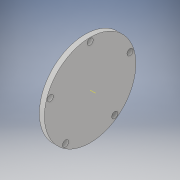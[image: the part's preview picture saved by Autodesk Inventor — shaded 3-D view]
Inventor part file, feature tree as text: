
AUTODESK INVENTOR PART (.ipt)
format: ipt  version: 2018 (Build 220112000, 112)  size: 112,128 bytes
history: native  units: in
note: dims shown in document units (in); Inventor stores cm internally (conversion verified against a paired STEP export)
features: extrude x2, sketch x2, other x1, pattern_circular x1
ambient origin geometry x8: Origin, YZ Plane, XZ Plane, XY Plane, X Axis, Y Axis, Z Axis, Center Point
bodies: Solid1 (feature_tree)
feature tree (6):
  extrude  "Extrusion1"  Depth=0.3937in TaperAngle=0.0deg
  extrude  "Extrusion2"  Depth=0.3937in
  other  "Work Axis1"
  pattern_circular  "Circular Pattern1"  [2 undecoded]
  sketch  "Sketch1"  dims[d0=7.0866in d1=0.3937in d2=0.0in]
  sketch  "Sketch2"  dims[d3=3.248in d4=0.4724in d5=0.3937in d6=0.0in d7=1.9685in d8=360.0deg]
note: 2 required parameter values undecoded (feature->parameter linkage not recoverable at this tier; creation-order binding heuristic only, values carry confidence <= 0.55)
